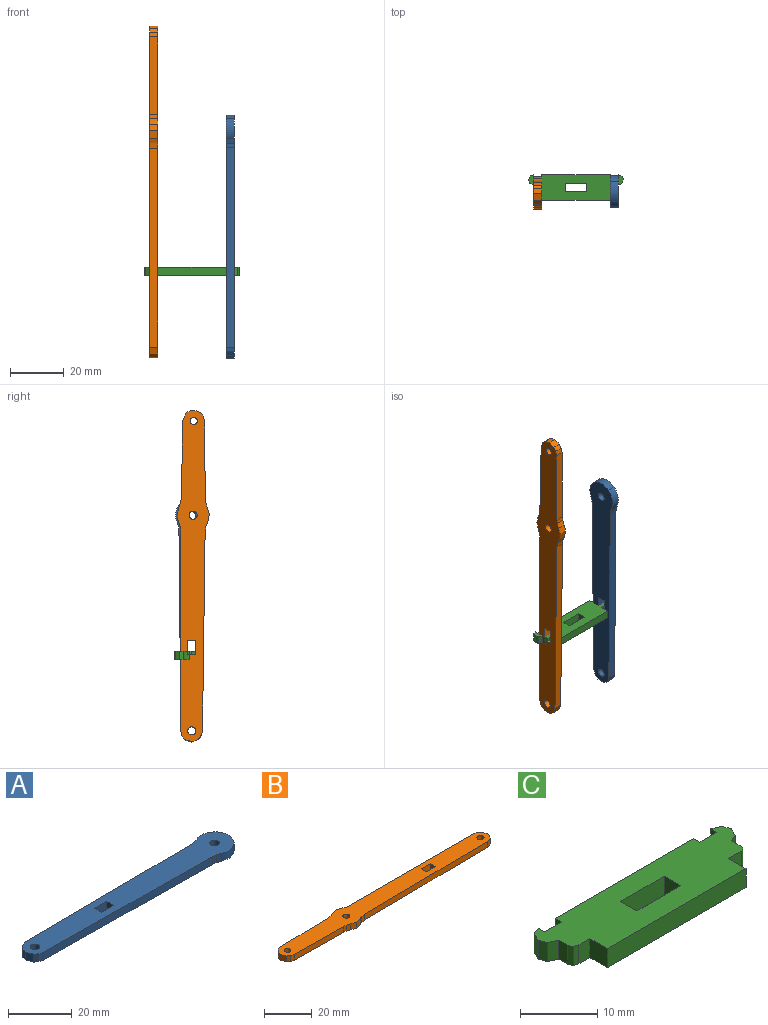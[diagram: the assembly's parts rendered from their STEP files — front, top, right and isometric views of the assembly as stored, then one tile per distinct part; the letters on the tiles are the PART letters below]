
ASSEMBLY  parts=3 mates=2
PART A: 23 faces, bbox 90.1x12x3 mm
  f0: plane 3x1.84mm, normal (-0.3,-0.95,0), area 5.8mm2, adj f1,f17,f20,f21
  f1: cylinder r=6mm len=7.21mm, axis (0,0,-1), area 24mm2, adj f0,f2,f20,f21
  f2: cylinder r=6mm len=7.42mm, axis (0,0,-1), area 24mm2, adj f1,f3,f20,f21
  f3: cylinder r=6mm len=7.21mm, axis (0,0,-1), area 24mm2, adj f2,f4,f20,f21
  f4: plane 3x1.43mm, normal (-0.32,0.95,0), area 4.5mm2, adj f3,f5,f20,f21
  f5: plane 3x1.92mm, normal (-0.12,0.99,0), area 5.8mm2, adj f4,f6,f20,f21
  f6: plane 74.29x3mm, normal (-0.01,1,0), area 222.9mm2, adj f5,f7,f20,f21
  f7: plane 3x2.53mm, normal (-0.35,0.94,0), area 8.1mm2, adj f6,f8,f20,f21
  f8: plane 3x1.35mm, normal (-0.79,0.61,0), area 5.1mm2, adj f7,f9,f20,f21
  f9: plane 3x1.72mm, normal (-0.98,0.22,0), area 5.3mm2, adj f8,f10,f20,f21
  f10: plane 3x2.54mm, normal (-0.94,-0.34,0), area 8.1mm2, adj f9,f11,f20,f21
  f11: plane 3x1.34mm, normal (-0.62,-0.78,0), area 5.1mm2, adj f10,f12,f20,f21
  f12: plane 3x1.71mm, normal (-0.23,-0.97,0), area 5.3mm2, adj f11,f13,f20,f21
  f13: plane 74.29x3mm, normal (-0.01,-1,0), area 222.9mm2, adj f12,f17,f20,f21
  f14: plane 3.1x3mm, normal (1,0,0), area 9.3mm2, adj f15,f18,f20,f21
  f15: plane 5.37x3mm, normal (0,-1,0), area 16.1mm2, adj f14,f16,f20,f21
  f16: plane 3.1x3mm, normal (-1,0,0), area 9.3mm2, adj f15,f18,f20,f21
  f17: plane 3x1.51mm, normal (-0.1,-1,0), area 4.5mm2, adj f0,f13,f20,f21
  f18: plane 5.37x3mm, normal (0,1,0), area 16.1mm2, adj f14,f16,f20,f21
  f19: cylinder r=1.5mm len=3mm, axis (0,0,-1), area 28.3mm2, adj f20,f21
  f20: plane 90.1x12mm, normal (0,0,1), area 760.4mm2, adj f0,f1,f2,f3,f4,f5,f6,f7
  f21: plane 90.1x12mm, normal (0,0,-1), area 760.4mm2, adj f0,f1,f2,f3,f4,f5,f6,f7
  f22: cylinder r=1.5mm len=3mm, axis (0,0,1), area 28.3mm2, adj f20,f21
PART B: 41 faces, bbox 123.1x12x3 mm
  f0: plane 3.1x3mm, normal (-1,0,0), area 9.3mm2, adj f1,f35,f39,f40
  f1: plane 5.37x3mm, normal (0,1,0), area 16.1mm2, adj f0,f2,f39,f40
  f2: plane 3.1x3mm, normal (1,0,0), area 9.3mm2, adj f1,f35,f39,f40
  f3: plane 3x1.71mm, normal (-0.23,-0.97,0), area 5.3mm2, adj f4,f36,f39,f40
  f4: plane 3x0.1mm, normal (0,-1,0), area 0.3mm2, adj f3,f5,f39,f40
  f5: plane 28.82x3mm, normal (-0.01,-1,0), area 86.5mm2, adj f4,f6,f39,f40
  f6: plane 3x1.6mm, normal (-0.11,-0.99,0), area 4.8mm2, adj f5,f7,f39,f40
  f7: plane 3x1.93mm, normal (-0.33,-0.94,0), area 6.1mm2, adj f6,f8,f39,f40
  f8: plane 3x0.06mm, normal (-0.16,-0.99,0), area 0.2mm2, adj f7,f9,f39,f40
  f9: plane 3x2.39mm, normal (-0.27,-0.96,0), area 7.4mm2, adj f8,f10,f39,f40
  f10: plane 3.06x3mm, normal (0.2,-0.98,0), area 9.4mm2, adj f9,f11,f39,f40
  f11: plane 3x0.06mm, normal (0.74,0.67,0), area 0.3mm2, adj f10,f12,f39,f40
  f12: plane 3x1.51mm, normal (0.37,-0.93,0), area 4.9mm2, adj f11,f13,f39,f40
  f13: plane 3x2.05mm, normal (0.14,-0.99,0), area 6.2mm2, adj f12,f14,f39,f40
  f14: plane 73.74x3mm, normal (0.01,-1,0), area 221.2mm2, adj f13,f15,f39,f40
  f15: plane 3x2.54mm, normal (0.35,-0.94,0), area 8.1mm2, adj f14,f16,f39,f40
  f16: plane 3x1.35mm, normal (0.79,-0.61,0), area 5.1mm2, adj f15,f17,f39,f40
  f17: plane 3x1.72mm, normal (0.98,-0.21,0), area 5.3mm2, adj f16,f18,f39,f40
  f18: plane 3x2.54mm, normal (0.94,0.34,0), area 8.1mm2, adj f17,f19,f39,f40
  f19: plane 3x1.35mm, normal (0.61,0.79,0), area 5.1mm2, adj f18,f20,f39,f40
  f20: plane 3x1.72mm, normal (0.22,0.98,0), area 5.3mm2, adj f19,f21,f39,f40
  f21: plane 73.75x3mm, normal (0,1,0), area 221.2mm2, adj f20,f22,f39,f40
  f22: plane 3x1.62mm, normal (0.1,0.99,0), area 4.9mm2, adj f21,f23,f39,f40
  f23: plane 3x1.95mm, normal (0.33,0.94,0), area 6.2mm2, adj f22,f24,f39,f40
  f24: plane 3x2.39mm, normal (0.25,0.97,0), area 7.4mm2, adj f23,f25,f39,f40
  f25: plane 3.06x3mm, normal (-0.21,0.98,0), area 9.4mm2, adj f24,f26,f39,f40
  f26: plane 3x1.49mm, normal (-0.37,0.93,0), area 4.8mm2, adj f25,f27,f39,f40
  f27: plane 3x2.02mm, normal (-0.15,0.99,0), area 6.1mm2, adj f26,f28,f39,f40
  f28: plane 28.81x3mm, normal (-0.02,1,0), area 86.5mm2, adj f27,f29,f39,f40
  f29: plane 3x0.1mm, normal (0,1,0), area 0.3mm2, adj f28,f30,f39,f40
  f30: plane 3x2.51mm, normal (-0.36,0.93,0), area 8.1mm2, adj f29,f31,f39,f40
  f31: plane 3x1.35mm, normal (-0.8,0.6,0), area 5.1mm2, adj f30,f32,f39,f40
  f32: plane 3x1.71mm, normal (-0.98,0.21,0), area 5.3mm2, adj f31,f33,f39,f40
  f33: plane 3x2.53mm, normal (-0.94,-0.34,0), area 8.1mm2, adj f32,f36,f39,f40
  f34: cylinder r=1.5mm len=3mm, axis (0,0,-1), area 28.3mm2, adj f39,f40
  f35: plane 5.37x3mm, normal (0,-1,0), area 16.1mm2, adj f0,f2,f39,f40
  f36: plane 3x1.33mm, normal (-0.62,-0.79,0), area 5.1mm2, adj f3,f33,f39,f40
  f37: cylinder r=1.5mm len=3mm, axis (0,0,-1), area 28.3mm2, adj f39,f40
  f38: cylinder r=1.32mm len=3mm, axis (0,0,-1), area 25mm2, adj f39,f40
  f39: plane 123.1x12.02mm, normal (0,0,1), area 1011mm2, adj f0,f1,f2,f3,f4,f5,f6,f7
  f40: plane 123.1x12.02mm, normal (0,0,-1), area 1011mm2, adj f0,f1,f2,f3,f4,f5,f6,f7
PART C: 32 faces, bbox 35.3x9.5x3 mm
  f0: plane 3x3mm, normal (1,0,0), area 9mm2, adj f1,f29,f30,f31
  f1: plane 8x3mm, normal (0,-1,0), area 24mm2, adj f0,f2,f30,f31
  f2: plane 3x3mm, normal (-1,0,0), area 9mm2, adj f1,f29,f30,f31
  f3: plane 3x1.18mm, normal (0.36,-0.93,0), area 3.8mm2, adj f4,f28,f30,f31
  f4: plane 3x1.42mm, normal (0.9,-0.44,0), area 4.7mm2, adj f3,f5,f30,f31
  f5: plane 3x1.25mm, normal (0.93,0.38,0), area 4mm2, adj f4,f6,f30,f31
  f6: plane 3x1.37mm, normal (0.42,0.91,0), area 4.5mm2, adj f5,f7,f30,f31
  f7: plane 3x1.12mm, normal (-1,0,0), area 3.4mm2, adj f6,f8,f30,f31
  f8: plane 3.1x3mm, normal (0,1,0), area 9.3mm2, adj f7,f9,f30,f31
  f9: plane 3x1.13mm, normal (1,0,0), area 3.4mm2, adj f8,f10,f30,f31
  f10: plane 25.3x3mm, normal (0,1,0), area 75.9mm2, adj f9,f11,f30,f31
  f11: plane 3x1.13mm, normal (-1,0,0), area 3.4mm2, adj f10,f12,f30,f31
  f12: plane 3.1x3mm, normal (0,1,0), area 9.3mm2, adj f11,f13,f30,f31
  f13: plane 3x1.11mm, normal (1,0,0), area 3.3mm2, adj f12,f14,f30,f31
  f14: plane 3x1.18mm, normal (-0.32,0.95,0), area 3.8mm2, adj f13,f15,f30,f31
  f15: plane 3x1.47mm, normal (-0.9,0.43,0), area 4.9mm2, adj f14,f16,f30,f31
  f16: plane 3x1.24mm, normal (-0.94,-0.34,0), area 3.9mm2, adj f15,f17,f30,f31
  f17: plane 3x1.43mm, normal (-0.41,-0.91,0), area 4.7mm2, adj f16,f18,f30,f31
  f18: plane 3x1.6mm, normal (-1,0,0), area 4.8mm2, adj f17,f19,f30,f31
  f19: plane 3x0.74mm, normal (-0.92,-0.39,0), area 2.4mm2, adj f18,f20,f30,f31
  f20: plane 3x0.79mm, normal (-0.29,-0.96,0), area 2.5mm2, adj f19,f21,f30,f31
  f21: plane 3x2mm, normal (0,-1,0), area 6mm2, adj f20,f22,f30,f31
  f22: plane 3.21x3mm, normal (-1,0,0), area 9.6mm2, adj f21,f23,f30,f31
  f23: plane 25.3x3mm, normal (0,-1,0), area 75.9mm2, adj f22,f24,f30,f31
  f24: plane 3.21x3mm, normal (1,0,0), area 9.6mm2, adj f23,f25,f30,f31
  f25: plane 3x2.31mm, normal (0,-1,0), area 6.9mm2, adj f24,f26,f30,f31
  f26: plane 3x0.49mm, normal (0.29,-0.96,0), area 1.5mm2, adj f25,f27,f30,f31
  f27: plane 3x0.63mm, normal (0.9,-0.44,0), area 2.1mm2, adj f26,f28,f30,f31
  f28: plane 3x1.8mm, normal (1,0,0), area 5.4mm2, adj f3,f27,f30,f31
  f29: plane 8x3mm, normal (0,1,0), area 24mm2, adj f0,f2,f30,f31
  f30: plane 35.25x9.54mm, normal (0,0,1), area 259mm2, adj f0,f1,f2,f3,f4,f5,f6,f7
  f31: plane 35.25x9.54mm, normal (0,0,-1), area 259mm2, adj f0,f1,f2,f3,f4,f5,f6,f7
PLACE A rot(axis=(0,-1,0),90deg) t=(15.65,-78.74,63.83)mm
PLACE B rot(axis=(0,1,0),90deg) t=(-15.65,-90.44,-33.53)mm
PLACE C t=(19.63,-42.58,0)mm
MATE fastened A.f22 <-> B.f34  axis (-1,0,0) through (12.65,-1.81,-26.61)mm
MATE fastened A.f20 <-> C.f24  axis (-1,0,0) through (12.65,-1.81,1.5)mm
